# Revit family: Sink-Undermount-Kitchen-KOHLER-DICKINSON-K-6546
name_source: partatom
category: Plumbing Fixtures
revit_build: Autodesk Revit 2017 (Build: 20160225_1515(x64)
units: mm (PartAtom-declared; Revit-internal decimal feet)

## family parameters
Cut with Voids When Loaded = No
Host = Face
OmniClass Number = 23.31.13.00
OmniClass Title = Sinks
Part Type = Normal
Room Calculation Point = No
Round Connector Dimension = Use Diameter
Shared = No

## types (3) — shared parameters
ADA Compliant = No
Assembly Code = D2010400
CW Connection = No
Cold Water Inlet = Cold Water Inlet
Date Modified = 12/02/2020
Default Elevation = 36"
Description = Under Counter Apron Sink
Drain Included = No
HW Connection = No
Height = 8 1/2"
Hot Water Inlet = Hot Water Inlet
Length = 19 9/16"
Manufacturer = KOHLER Co.
Master Format 2014 Name = Residential Lavatories and Sinks
MasterFormat 2014 = 22 41 16
Material = Enameled Cast Iron
Product Name = DICKINSON
URL = https://www.us.kohler.com
Vent Connection = No
Waste Connection = Yes
Waste Water Outlet = Waste Water Outlet
WaterSense Certified = No
Width = 33"

## per-type parameters (varying)
| type | Finish | Model | Type |
| 0-White | KOHLER-Enameled_Cast_Iron-0-White | K-6546-0 | 1 |
| 7-Black Black | KOHLER-Enameled_Cast_Iron-7-Black_Black | K-6546-7 | 2 |
| 96-Biscuit | KOHLER-Enameled_Cast_Iron-96-Biscuit | K-6546-96 | 3 |

## geometry (parser evidence)
native form markers: Sweep x4
no freeform markers — native parametric forms only
